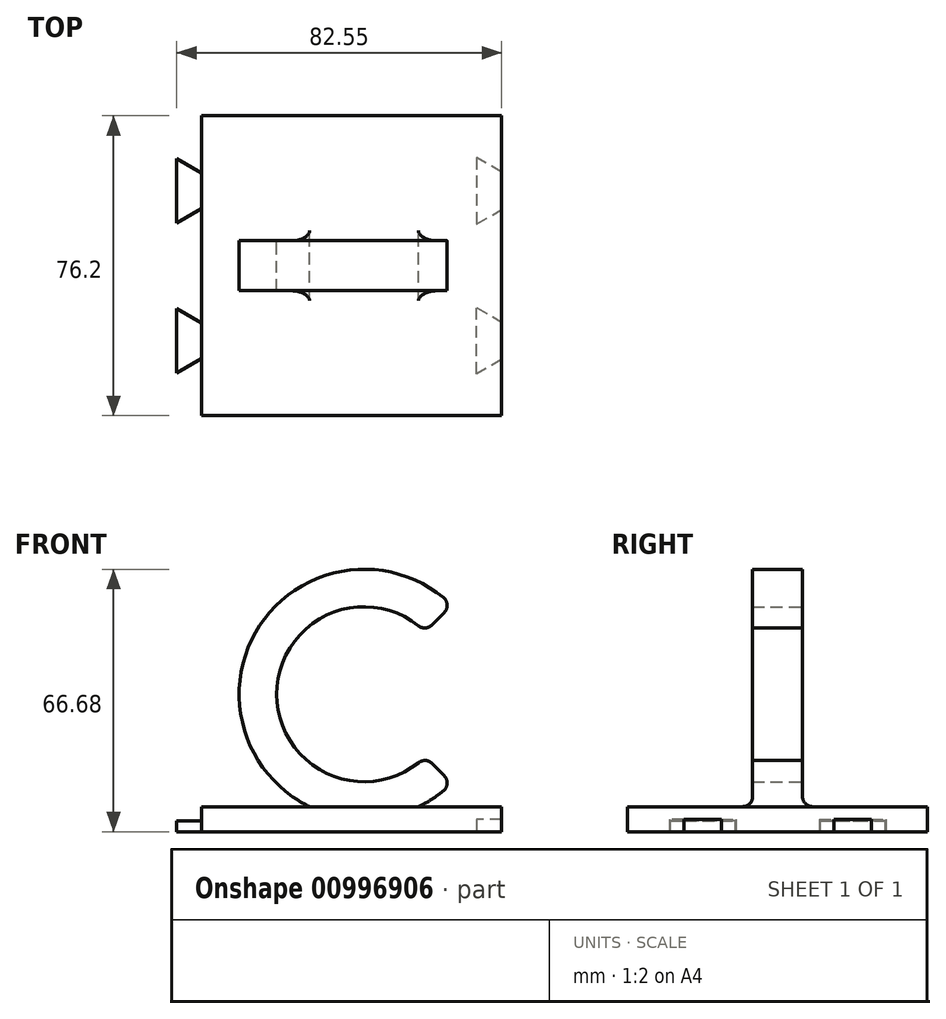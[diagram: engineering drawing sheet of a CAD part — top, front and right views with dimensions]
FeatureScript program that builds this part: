
annotation { "Feature Type Name" : "Feature", "Feature Type Description" : "" }
export const myFeature = defineFeature(function(context is Context, id is Id, definition is map)
    precondition{}
    {
        {
            var Q0;
            Q0=qCreatedBy(makeId("Top.planeOp"),FACE);
            var sketch = newSketch(context, id + "F0", { "sketchPlane" : qUnion([Q0])});
            skLineSegment(sketch, "E0.bottom", {"start": v(38.1, -38.1) * mm, "end": v(-38.1, -38.1) * mm});
            skLineSegment(sketch, "E0.top", {"start": v(38.1, 38.1) * mm, "end": v(-38.1, 38.1) * mm});
            skLineSegment(sketch, "E0.left", {"start": v(38.1, -38.1) * mm, "end": v(38.1, 38.1) * mm});
            skLineSegment(sketch, "E0.right", {"start": v(-38.1, -38.1) * mm, "end": v(-38.1, 38.1) * mm});
            skPoint(sketch, "E0.middle", {"position": v(0, 0) * mm});
            skSolve(sketch);
        }
        {
            var Q0;
            Q0=qCreatedBy(makeId("Front.planeOp"),FACE);
            var sketch = newSketch(context, id + "F1", { "sketchPlane" : qUnion([Q0])});
            skArc(sketch, "E1", {"start": v(25.4, 51.25) * mm, "mid": v(-28.58, 28.58) * mm, "end": v(25.4, 5.9) * mm});
            skLineSegment(sketch, "E2", {"start": v(16.41, 60.33) * mm, "end": v(-26.64, 60.33) * mm, "construction": true});
            skLineSegment(sketch, "E3", {"start": v(-19.56, -3.18) * mm, "end": v(26.32, -3.17) * mm, "construction": true});
            skArc(sketch, "E4", {"start": v(18.73, 44.45) * mm, "mid": v(-19.05, 28.58) * mm, "end": v(18.73, 12.7) * mm});
            skLineSegment(sketch, "E5", {"start": v(25.4, 51.25) * mm, "end": v(18.73, 44.45) * mm});
            skLineSegment(sketch, "E6", {"start": v(18.73, 12.7) * mm, "end": v(25.4, 5.9) * mm});
            skLineSegment(sketch, "E7", {"start": v(18.73, 44.45) * mm, "end": v(34.7, 28.8) * mm, "construction": true});
            skSolve(sketch);
        }
        {
            var Q0;
            Q0=qSketchRegion(id+"F0",true);
            extrude(context, id + "F2", {"entities" : qUnion([Q0]), "oppositeDirection" : true, "depth" : 6.35 * mm, "offsetDistance" : 25.4 * mm});
        }
        {
            var Q0;
            Q0=qSketchRegion(id+"F1",true);
            extrude(context, id + "F3", {"entities" : qUnion([Q0]), "operationType" : NewBodyOperationType.ADD, "endBound" : BoundingType.SYMMETRIC, "depth" : 12.7 * mm, "offsetDistance" : 25.4 * mm});
        }
        {
            var Q0;
            Q0=makeQuery(id+"F3.opExtrude","SWEPT_EDGE",EDGE,{"disambiguationData":[OSD([sQuery(id+"F1.wireOp",EDGE,"E1"),sQuery(id+"F1.wireOp",EDGE,"E5")])]});
            var Q1;
            Q1=makeQuery(id+"F3.opExtrude","SWEPT_EDGE",EDGE,{"disambiguationData":[OSD([sQuery(id+"F1.wireOp",EDGE,"E4"),sQuery(id+"F1.wireOp",EDGE,"E5")])]});
            var Q2;
            Q2=makeQuery(id+"F3.opExtrude","SWEPT_EDGE",EDGE,{"disambiguationData":[OSD([sQuery(id+"F1.wireOp",EDGE,"E4"),sQuery(id+"F1.wireOp",EDGE,"E6")])]});
            var Q3;
            Q3=makeQuery(id+"F3.opExtrude","SWEPT_EDGE",EDGE,{"disambiguationData":[OSD([sQuery(id+"F1.wireOp",EDGE,"E1"),sQuery(id+"F1.wireOp",EDGE,"E6")])]});
            var Q4;
            Q4=makeQuery(id+"F3.boolean.opBoolean","INTERSECT",EDGE,{"derivedFrom":[makeQuery(id+"F2.opExtrude","CAP_FACE",FACE,{"disambiguationData":[OSD([sQuery(id+"F0.wireOp",EDGE,"E0.bottom"),sQuery(id+"F0.wireOp",EDGE,"E0.top"),sQuery(id+"F0.wireOp",EDGE,"E0.left"),sQuery(id+"F0.wireOp",EDGE,"E0.right")])],"isStart":true}),makeQuery(id+"F3.opExtrude","CAP_FACE",FACE,{"disambiguationData":[OSD([sQuery(id+"F1.wireOp",EDGE,"E1"),sQuery(id+"F1.wireOp",EDGE,"E4"),sQuery(id+"F1.wireOp",EDGE,"E5"),sQuery(id+"F1.wireOp",EDGE,"E6")])],"isStart":false})]});
            var Q5;
            Q5=makeQuery(id+"F3.boolean.opBoolean","INTERSECT",EDGE,{"derivedFrom":[makeQuery(id+"F2.opExtrude","CAP_FACE",FACE,{"disambiguationData":[OSD([sQuery(id+"F0.wireOp",EDGE,"E0.bottom"),sQuery(id+"F0.wireOp",EDGE,"E0.top"),sQuery(id+"F0.wireOp",EDGE,"E0.left"),sQuery(id+"F0.wireOp",EDGE,"E0.right")])],"isStart":true}),makeQuery(id+"F3.opExtrude","CAP_FACE",FACE,{"disambiguationData":[OSD([sQuery(id+"F1.wireOp",EDGE,"E1"),sQuery(id+"F1.wireOp",EDGE,"E4"),sQuery(id+"F1.wireOp",EDGE,"E5"),sQuery(id+"F1.wireOp",EDGE,"E6")])],"isStart":true})]});
            fillet(context, id + "F4", {"entities" : qUnion([Q0, Q1, Q2, Q3, Q4, Q5]), "radius" : 2.54 * mm, "tangentPropagation" : true, "allowEdgeOverflow" : false});
        }
        {
            var Q0;
            Q0=makeQuery(id+"F2.opExtrude","CAP_FACE",FACE,{"disambiguationData":[OSD([sQuery(id+"F0.wireOp",EDGE,"E0.bottom"),sQuery(id+"F0.wireOp",EDGE,"E0.top"),sQuery(id+"F0.wireOp",EDGE,"E0.left"),sQuery(id+"F0.wireOp",EDGE,"E0.right")])],"isStart":false});
            var sketch = newSketch(context, id + "F5", { "sketchPlane" : qUnion([Q0])});
            skLineSegment(sketch, "E8", {"start": v(38.1, 23.81) * mm, "end": v(31.75, 27.48) * mm});
            skLineSegment(sketch, "E9", {"start": v(31.75, 27.48) * mm, "end": v(31.75, 10.62) * mm});
            skLineSegment(sketch, "E10", {"start": v(31.75, 10.62) * mm, "end": v(38.1, 14.29) * mm});
            skLineSegment(sketch, "E11", {"start": v(38.1, 14.29) * mm, "end": v(38.1, 23.81) * mm});
            skLineSegment(sketch, "E12", {"start": v(38.1, 19.05) * mm, "end": v(38.1, 38.1) * mm, "construction": true});
            skLineSegment(sketch, "E13.MirrorCS", {"start": v(31.75, -27.48) * mm, "end": v(31.75, -10.62) * mm});
            skLineSegment(sketch, "E14.MirrorCS", {"start": v(38.1, -23.81) * mm, "end": v(31.75, -27.48) * mm});
            skLineSegment(sketch, "E15.MirrorCS", {"start": v(38.1, -14.29) * mm, "end": v(38.1, -23.81) * mm});
            skLineSegment(sketch, "E16.MirrorCS", {"start": v(31.75, -10.62) * mm, "end": v(38.1, -14.29) * mm});
            skSolve(sketch);
        }
        {
            var Q0;
            Q0=qSketchRegion(id+"F5",true);
            extrude(context, id + "F6", {"entities" : qUnion([Q0]), "operationType" : NewBodyOperationType.REMOVE, "oppositeDirection" : true, "depth" : 3.17 * mm, "offsetDistance" : 25.4 * mm});
        }
        {
            var Q0;
            Q0=makeQuery(id+"F2.opExtrude","CAP_FACE",FACE,{"disambiguationData":[OSD([sQuery(id+"F0.wireOp",EDGE,"E0.bottom"),sQuery(id+"F0.wireOp",EDGE,"E0.top"),sQuery(id+"F0.wireOp",EDGE,"E0.left"),sQuery(id+"F0.wireOp",EDGE,"E0.right")])],"isStart":false});
            var sketch = newSketch(context, id + "F7", { "sketchPlane" : qUnion([Q0])});
            skLineSegment(sketch, "E17", {"start": v(-38.1, 23.61) * mm, "end": v(-38.1, 14.49) * mm});
            skLineSegment(sketch, "E18", {"start": v(-38.1, 14.49) * mm, "end": v(-44.45, 10.82) * mm});
            skLineSegment(sketch, "E19", {"start": v(-44.45, 10.82) * mm, "end": v(-44.45, 27.28) * mm});
            skLineSegment(sketch, "E20", {"start": v(-44.45, 27.28) * mm, "end": v(-38.1, 23.61) * mm});
            skLineSegment(sketch, "E21", {"start": v(-38.1, 19.05) * mm, "end": v(-38.1, 38.1) * mm, "construction": true});
            skLineSegment(sketch, "E22.MirrorCS", {"start": v(-38.1, -14.49) * mm, "end": v(-44.45, -10.82) * mm});
            skLineSegment(sketch, "E23.MirrorCS", {"start": v(-44.45, -10.82) * mm, "end": v(-44.45, -27.28) * mm});
            skLineSegment(sketch, "E24.MirrorCS", {"start": v(-38.1, -23.61) * mm, "end": v(-38.1, -14.49) * mm});
            skLineSegment(sketch, "E25.MirrorCS", {"start": v(-44.45, -27.28) * mm, "end": v(-38.1, -23.61) * mm});
            skSolve(sketch);
        }
        {
            var Q0;
            Q0 = qSketchRegion(id + "F7", true);
            extrude(context, id + "F8", {"entities" : qUnion([Q0]), "operationType" : NewBodyOperationType.ADD, "oppositeDirection" : true, "depth" : 2.78 * mm, "offsetDistance" : 25.4 * mm});
        }
    });
